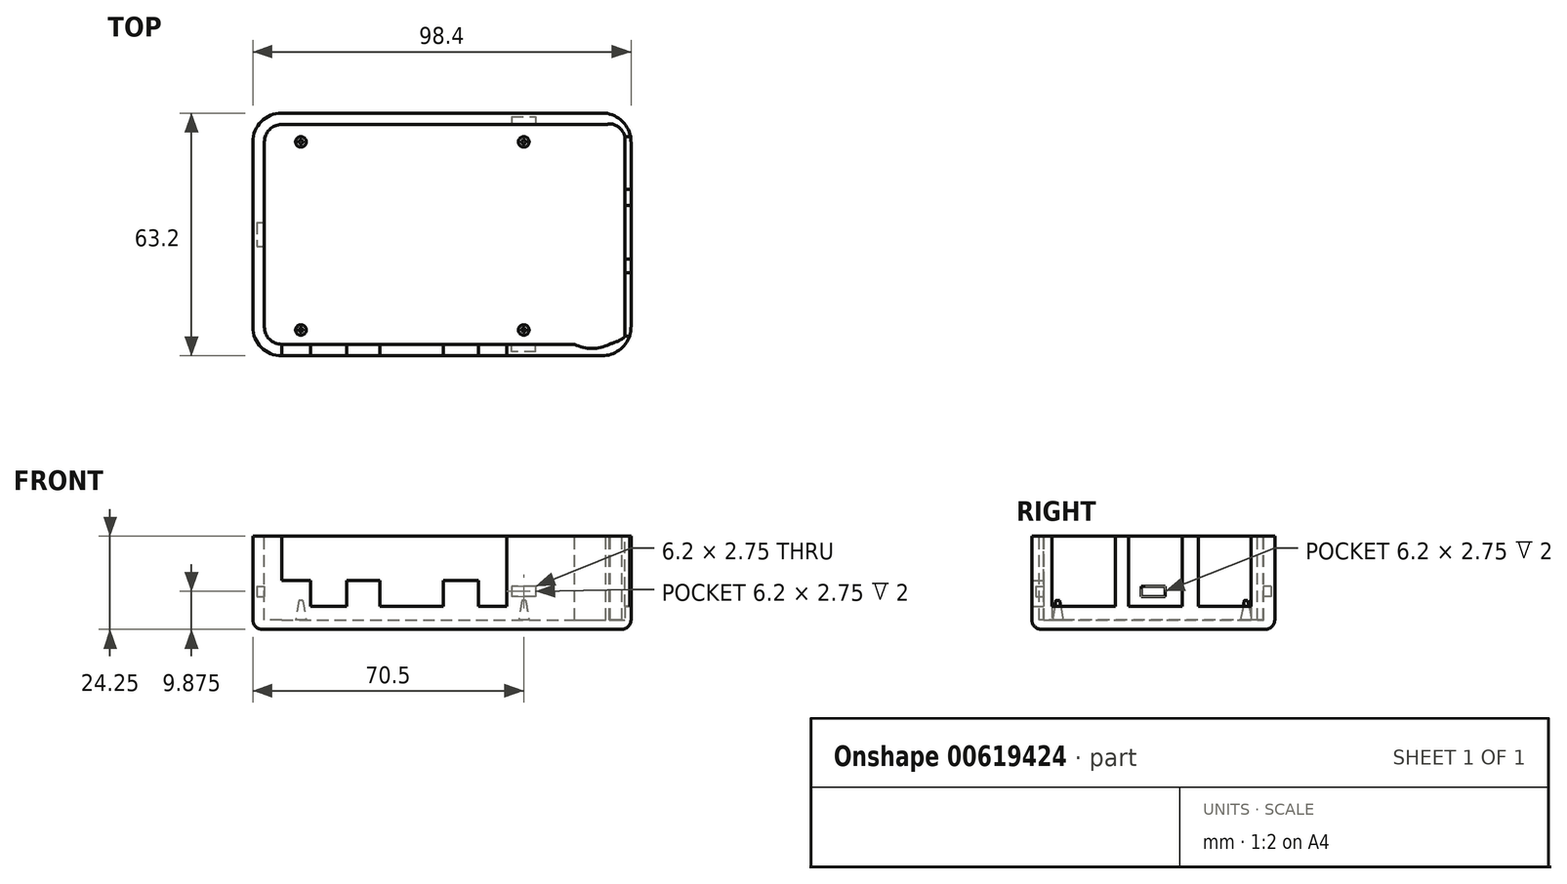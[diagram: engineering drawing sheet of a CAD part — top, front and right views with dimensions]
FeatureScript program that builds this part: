
annotation { "Feature Type Name" : "Feature", "Feature Type Description" : "" }
export const myFeature = defineFeature(function(context is Context, id is Id, definition is map)
    precondition{}
    {
        {
            var Q0;
            Q0=qCreatedBy(makeId("Top.planeOp"),FACE);
            var sketch = newSketch(context, id + "F0", { "sketchPlane" : qUnion([Q0])});
            skLineSegment(sketch, "E0.bottom", {"start": v(2.5, 0) * mm, "end": v(85.9, 0) * mm});
            skLineSegment(sketch, "E0.top", {"start": v(2.5, 53.2) * mm, "end": v(85.9, 53.2) * mm});
            skLineSegment(sketch, "E0.left", {"start": v(0, 2.5) * mm, "end": v(0, 50.7) * mm});
            skLineSegment(sketch, "E0.right", {"start": v(88.4, 2.5) * mm, "end": v(88.4, 50.7) * mm});
            skPoint(sketch, "E1.visualSharp", {"position": v(0, 53.2) * mm});
            skArc(sketch, "E1.filletArc", {"start": v(2.5, 53.2) * mm, "mid": v(0.73, 52.47) * mm, "end": v(0, 50.7) * mm});
            skPoint(sketch, "E2.visualSharp", {"position": v(0, 0) * mm});
            skArc(sketch, "E2.filletArc", {"start": v(0, 2.5) * mm, "mid": v(0.73, 0.73) * mm, "end": v(2.5, 0) * mm});
            skPoint(sketch, "E3.visualSharp", {"position": v(88.4, 0) * mm});
            skArc(sketch, "E3.filletArc", {"start": v(85.9, 0) * mm, "mid": v(87.67, 0.73) * mm, "end": v(88.4, 2.5) * mm});
            skPoint(sketch, "E4.visualSharp", {"position": v(88.4, 53.2) * mm});
            skArc(sketch, "E4.filletArc", {"start": v(88.4, 50.7) * mm, "mid": v(87.67, 52.47) * mm, "end": v(85.9, 53.2) * mm});
            skArc(sketch, "E5.0", {"start": v(2.5, 54.2) * mm, "mid": v(0.03, 53.17) * mm, "end": v(-1, 50.7) * mm});
            skLineSegment(sketch, "E5.1", {"start": v(-1, 2.5) * mm, "end": v(-1, 50.7) * mm});
            skLineSegment(sketch, "E5.2", {"start": v(2.5, 54.2) * mm, "end": v(85.9, 54.2) * mm});
            skArc(sketch, "E5.3", {"start": v(-1, 2.5) * mm, "mid": v(0.03, 0.03) * mm, "end": v(2.5, -1) * mm});
            skArc(sketch, "E5.4", {"start": v(89.4, 50.7) * mm, "mid": v(88.37, 53.17) * mm, "end": v(85.9, 54.2) * mm});
            skLineSegment(sketch, "E5.5", {"start": v(89.4, 2.5) * mm, "end": v(89.4, 50.7) * mm});
            skArc(sketch, "E5.6", {"start": v(85.9, -1) * mm, "mid": v(88.37, 0.03) * mm, "end": v(89.4, 2.5) * mm});
            skLineSegment(sketch, "E5.7", {"start": v(2.5, -1) * mm, "end": v(85.9, -1) * mm});
            skLineSegment(sketch, "E6.0", {"start": v(2.5, 58.2) * mm, "end": v(85.9, 58.2) * mm});
            skArc(sketch, "E6.1", {"start": v(93.4, 50.7) * mm, "mid": v(91.2, 56) * mm, "end": v(85.9, 58.2) * mm});
            skArc(sketch, "E6.2", {"start": v(2.5, 58.2) * mm, "mid": v(-2.8, 56) * mm, "end": v(-5, 50.7) * mm});
            skLineSegment(sketch, "E6.3", {"start": v(93.4, 2.5) * mm, "end": v(93.4, 50.7) * mm});
            skLineSegment(sketch, "E6.4", {"start": v(-5, 2.5) * mm, "end": v(-5, 50.7) * mm});
            skArc(sketch, "E6.5", {"start": v(-5, 2.5) * mm, "mid": v(-2.8, -2.8) * mm, "end": v(2.5, -5) * mm});
            skLineSegment(sketch, "E6.6", {"start": v(2.5, -5) * mm, "end": v(85.9, -5) * mm});
            skArc(sketch, "E6.7", {"start": v(85.9, -5) * mm, "mid": v(91.2, -2.8) * mm, "end": v(93.4, 2.5) * mm});
            skLineSegment(sketch, "E7", {"start": v(-2.22, 61) * mm, "end": v(-16.8, 62.79) * mm, "construction": true});
            skSolve(sketch);
        }
        {
            var Q0;
            Q0=makeQuery(id+"F0.imprint","IMPRINT",FACE,{"disambiguationData":[TD([[makeQuery(id+"F0.imprint","IMPRINT",EDGE,{"derivedFrom":sQuery(id+"F0.wireOp",EDGE,"E5.0")}),-1.0]])]});
            var Q1;
            Q1=makeQuery(id+"F0.imprint","IMPRINT",FACE,{"disambiguationData":[TD([[makeQuery(id+"F0.imprint","IMPRINT",EDGE,{"derivedFrom":sQuery(id+"F0.wireOp",EDGE,"E0.bottom")}),-1.0]])]});
            var Q2;
            Q2=makeQuery(id+"F0.imprint","IMPRINT",FACE,{"disambiguationData":[TD([[makeQuery(id+"F0.imprint","IMPRINT",EDGE,{"derivedFrom":sQuery(id+"F0.wireOp",EDGE,"E0.bottom")}),1.0]])]});
            extrude(context, id + "F1", {"entities" : qUnion([Q0, Q1, Q2]), "depth" : 21.25 * mm, "offsetDistance" : 25 * mm});
        }
        {
            var Q0;
            Q0=makeQuery(id+"F1.opExtrude","CAP_EDGE",EDGE,{"disambiguationData":[OSD([sQuery(id+"F0.wireOp",EDGE,"E6.1")])],"isStart":true});
            var Q1;
            Q1=makeQuery(id+"F1.opExtrude","CAP_EDGE",EDGE,{"disambiguationData":[OSD([sQuery(id+"F0.wireOp",EDGE,"E6.0")])],"isStart":true});
            var Q2;
            Q2=makeQuery(id+"F1.opExtrude","CAP_EDGE",EDGE,{"disambiguationData":[OSD([sQuery(id+"F0.wireOp",EDGE,"E6.3")])],"isStart":true});
            fillet(context, id + "F2", {"entities" : qUnion([Q0, Q1, Q2]), "radius" : 2.5 * mm, "tangentPropagation" : true, "allowEdgeOverflow" : false});
        }
        {
            var Q0;
            Q0=makeQuery(id+"F1.opExtrude","CAP_FACE",FACE,{"disambiguationData":[OSD([sQuery(id+"F0.wireOp",EDGE,"E6.0"),sQuery(id+"F0.wireOp",EDGE,"E6.1"),sQuery(id+"F0.wireOp",EDGE,"E6.2"),sQuery(id+"F0.wireOp",EDGE,"E6.3"),sQuery(id+"F0.wireOp",EDGE,"E6.4"),sQuery(id+"F0.wireOp",EDGE,"E6.5"),sQuery(id+"F0.wireOp",EDGE,"E6.6"),sQuery(id+"F0.wireOp",EDGE,"E6.7")])],"isStart":false});
            var sketch = newSketch(context, id + "F3", { "sketchPlane" : qUnion([Q0])});
            skLineSegment(sketch, "E8.0", {"start": v(-2, 2.5) * mm, "end": v(-2, 50.7) * mm});
            skArc(sketch, "E8.2", {"start": v(-2, 2.5) * mm, "mid": v(-0.68, -0.68) * mm, "end": v(2.5, -2) * mm});
            skLineSegment(sketch, "E8.3", {"start": v(2.5, 55.2) * mm, "end": v(86.9, 55.2) * mm});
            skLineSegment(sketch, "E8.4", {"start": v(2.5, -2) * mm, "end": v(86.9, -2) * mm});
            skPoint(sketch, "E9.visualSharp", {"position": v(-2, 55.2) * mm});
            skArc(sketch, "E9.filletArc", {"start": v(2.5, 55.2) * mm, "mid": v(-0.68, 53.88) * mm, "end": v(-2, 50.7) * mm});
            skPoint(sketch, "E10.visualSharp", {"position": v(91, 55.2) * mm});
            skArc(sketch, "E10.filletArc", {"start": v(91.4, 50.7) * mm, "mid": v(90.08, 53.88) * mm, "end": v(86.9, 55.2) * mm});
            skLineSegment(sketch, "E11", {"start": v(91.4, 2.5) * mm, "end": v(91.4, 50.7) * mm});
            skPoint(sketch, "E12.visualSharp", {"position": v(91.4, -2) * mm});
            skArc(sketch, "E12.filletArc", {"start": v(86.9, -2) * mm, "mid": v(90.08, -0.68) * mm, "end": v(91.4, 2.5) * mm});
            skSolve(sketch);
        }
        {
            var Q0;
            Q0=makeQuery(id+"F3.imprint","IMPRINT",FACE,{"disambiguationData":[TD([[makeQuery(id+"F3.imprint","IMPRINT",EDGE,{"derivedFrom":sQuery(id+"F3.wireOp",EDGE,"E8.0")}),-1.0]])]});
            extrude(context, id + "F4", {"entities" : qUnion([Q0]), "operationType" : NewBodyOperationType.REMOVE, "oppositeDirection" : true, "depth" : 18.75 * mm, "offsetDistance" : 25 * mm});
        }
        {
            var Q0;
            Q0=qCreatedBy(makeId("Top.planeOp"),FACE);
            var sketch = newSketch(context, id + "F5", { "sketchPlane" : qUnion([Q0])});
            skLineSegment(sketch, "E13.bottom", {"start": v(2.5, 0) * mm, "end": v(82.5, 0) * mm, "construction": true});
            skLineSegment(sketch, "E13.top", {"start": v(2.5, 56) * mm, "end": v(82.5, 56) * mm, "construction": true});
            skLineSegment(sketch, "E13.left", {"start": v(0, 2.5) * mm, "end": v(0, 53.5) * mm, "construction": true});
            skLineSegment(sketch, "E13.right", {"start": v(85, 2.5) * mm, "end": v(85, 53.5) * mm, "construction": true});
            skPoint(sketch, "E14.visualSharp", {"position": v(0, 56) * mm});
            skArc(sketch, "E14.filletArc", {"start": v(2.5, 56) * mm, "mid": v(0.73, 55.27) * mm, "end": v(0, 53.5) * mm, "construction": true});
            skPoint(sketch, "E15.visualSharp", {"position": v(85, 56) * mm});
            skArc(sketch, "E15.filletArc", {"start": v(85, 53.5) * mm, "mid": v(84.27, 55.27) * mm, "end": v(82.5, 56) * mm, "construction": true});
            skPoint(sketch, "E16.visualSharp", {"position": v(85, 0) * mm});
            skArc(sketch, "E16.filletArc", {"start": v(82.5, 0) * mm, "mid": v(84.27, 0.73) * mm, "end": v(85, 2.5) * mm, "construction": true});
            skPoint(sketch, "E17.visualSharp", {"position": v(0, 0) * mm});
            skArc(sketch, "E17.filletArc", {"start": v(0, 2.5) * mm, "mid": v(0.73, 0.73) * mm, "end": v(2.5, 0) * mm, "construction": true});
            skSolve(sketch);
        }
        {
            var Q0;
            Q0=makeQuery(id+"FpAsiEOdQiPqQSk_1.boolean.opBoolean","MERGE",FACE,{"derivedFrom":[makeQuery(id+"FFKmk7SwMBdEqLW_1.boolean.opBoolean","MERGE",FACE,{"derivedFrom":[makeQuery(id+"FIplIZIgQVPH8Ri_1.boolean.opBoolean","MERGE",FACE,{"derivedFrom":[makeQuery(id+"F4.boolean.opBoolean","COPY",FACE,{"derivedFrom":makeQuery(id+"F4.opExtrude","CAP_FACE",FACE,{"disambiguationData":[OSD([sQuery(id+"F3.wireOp",EDGE,"E8.0"),sQuery(id+"F3.wireOp",EDGE,"E8.1"),sQuery(id+"F3.wireOp",EDGE,"E8.2"),sQuery(id+"F3.wireOp",EDGE,"E8.3"),sQuery(id+"F3.wireOp",EDGE,"E8.4"),sQuery(id+"F3.wireOp",EDGE,"E8.5"),sQuery(id+"F3.wireOp",EDGE,"E8.6"),sQuery(id+"F3.wireOp",EDGE,"E8.7")])],"isStart":false})}),makeQuery(id+"FIplIZIgQVPH8Ri_1.opExtrude","CAP_FACE",FACE,{"disambiguationData":[OSD([sQuery(id+"FbSfHMxZk7SnYfS_1.wireOp",EDGE,"JDB0ovfy-WgS9-BKPD-cCMD-5imSfYRD1vYw.bottom"),sQuery(id+"FbSfHMxZk7SnYfS_1.wireOp",EDGE,"JDB0ovfy-WgS9-BKPD-cCMD-5imSfYRD1vYw.top"),sQuery(id+"FbSfHMxZk7SnYfS_1.wireOp",EDGE,"JDB0ovfy-WgS9-BKPD-cCMD-5imSfYRD1vYw.left"),sQuery(id+"FbSfHMxZk7SnYfS_1.wireOp",EDGE,"JDB0ovfy-WgS9-BKPD-cCMD-5imSfYRD1vYw.right")])],"isStart":false})]}),makeQuery(id+"FFKmk7SwMBdEqLW_1.opExtrude","CAP_FACE",FACE,{"disambiguationData":[OSD([sQuery(id+"FeB8znZlq4XmqRw_1.wireOp",EDGE,"MHbipOmZ-R87S-0nFG-E8Bu-bYtsTBabYH2Z.bottom"),sQuery(id+"FeB8znZlq4XmqRw_1.wireOp",EDGE,"MHbipOmZ-R87S-0nFG-E8Bu-bYtsTBabYH2Z.top"),sQuery(id+"FeB8znZlq4XmqRw_1.wireOp",EDGE,"MHbipOmZ-R87S-0nFG-E8Bu-bYtsTBabYH2Z.left"),sQuery(id+"FeB8znZlq4XmqRw_1.wireOp",EDGE,"MHbipOmZ-R87S-0nFG-E8Bu-bYtsTBabYH2Z.right")])],"isStart":false})]}),makeQuery(id+"FpAsiEOdQiPqQSk_1.opExtrude","CAP_FACE",FACE,{"disambiguationData":[OSD([sQuery(id+"Fj2ZZsyvJ0AxlN6_1.wireOp",EDGE,"Ikh8Ez46-MLNA-BZEZ-2Olo-oqhIJmUvsvPt.bottom"),sQuery(id+"Fj2ZZsyvJ0AxlN6_1.wireOp",EDGE,"Ikh8Ez46-MLNA-BZEZ-2Olo-oqhIJmUvsvPt.top"),sQuery(id+"Fj2ZZsyvJ0AxlN6_1.wireOp",EDGE,"Ikh8Ez46-MLNA-BZEZ-2Olo-oqhIJmUvsvPt.left"),sQuery(id+"Fj2ZZsyvJ0AxlN6_1.wireOp",EDGE,"Ikh8Ez46-MLNA-BZEZ-2Olo-oqhIJmUvsvPt.right")])],"isStart":false})]});
            var sketch = newSketch(context, id + "F6", { "sketchPlane" : qUnion([Q0])});
            skCircle(sketch, "E18", {"center": v(7.5, 1.7) * mm, "radius": 1.38 * mm});
            skCircle(sketch, "E19.0.1.0", {"center": v(7.5, 50.7) * mm, "radius": 1.38 * mm});
            skCircle(sketch, "E19.1.0.0", {"center": v(65.5, 1.7) * mm, "radius": 1.38 * mm});
            skCircle(sketch, "E19.1.1.0", {"center": v(65.5, 50.7) * mm, "radius": 1.38 * mm});
            skLineSegment(sketch, "E19.direction1", {"start": v(7.5, 1.7) * mm, "end": v(65.5, 1.7) * mm, "construction": true});
            skLineSegment(sketch, "E19.direction2", {"start": v(7.5, 1.7) * mm, "end": v(7.5, 50.7) * mm, "construction": true});
            skSolve(sketch);
        }
        {
            var Q0;
            Q0=makeQuery(id+"F4.boolean.opBoolean","COPY",FACE,{"derivedFrom":makeQuery(id+"F4.opExtrude","SWEPT_FACE",FACE,{"disambiguationData":[OSD([sQuery(id+"F3.wireOp",EDGE,"E8.0")])]})});
            var sketch = newSketch(context, id + "F7", { "sketchPlane" : qUnion([Q0])});
            skLineSegment(sketch, "E20.bottom", {"start": v(29.7, 11.25) * mm, "end": v(23.5, 11.25) * mm});
            skLineSegment(sketch, "E20.top", {"start": v(29.7, 8.5) * mm, "end": v(23.5, 8.5) * mm});
            skLineSegment(sketch, "E20.left", {"start": v(29.7, 11.25) * mm, "end": v(29.7, 8.5) * mm});
            skLineSegment(sketch, "E20.right", {"start": v(23.5, 11.25) * mm, "end": v(23.5, 8.5) * mm});
            skPoint(sketch, "E21", {"position": v(26.6, 11.25) * mm});
            skPoint(sketch, "E22", {"position": v(26.6, 8.5) * mm});
            skPoint(sketch, "E23", {"position": v(26.6, 21.25) * mm});
            skSolve(sketch);
        }
        {
            var Q0;
            Q0=makeQuery(id+"F7.imprint","IMPRINT",FACE,{"disambiguationData":[TD([[makeQuery(id+"F7.imprint","IMPRINT",EDGE,{"derivedFrom":sQuery(id+"F7.wireOp",EDGE,"E20.bottom")}),1.0]])]});
            extrude(context, id + "F8", {"entities" : qUnion([Q0]), "operationType" : NewBodyOperationType.REMOVE, "oppositeDirection" : true, "depth" : 2 * mm, "offsetDistance" : 25 * mm});
        }
        {
            var Q0;
            Q0=makeQuery(id+"F4.boolean.opBoolean","COPY",FACE,{"derivedFrom":makeQuery(id+"F4.opExtrude","SWEPT_FACE",FACE,{"disambiguationData":[OSD([sQuery(id+"F3.wireOp",EDGE,"E8.3")])]})});
            var sketch = newSketch(context, id + "F9", { "sketchPlane" : qUnion([Q0])});
            skLineSegment(sketch, "E24.bottom", {"start": v(62.4, 11.25) * mm, "end": v(68.6, 11.25) * mm});
            skLineSegment(sketch, "E24.top", {"start": v(62.4, 8.5) * mm, "end": v(68.6, 8.5) * mm});
            skLineSegment(sketch, "E24.left", {"start": v(62.4, 11.25) * mm, "end": v(62.4, 8.5) * mm});
            skLineSegment(sketch, "E24.right", {"start": v(68.6, 11.25) * mm, "end": v(68.6, 8.5) * mm});
            skLineSegment(sketch, "E25.0", {"start": v(64.12, 2.5) * mm, "end": v(66.88, 2.5) * mm, "construction": true});
            skPoint(sketch, "E26", {"position": v(65.5, 2.5) * mm});
            skPoint(sketch, "E27", {"position": v(65.5, 8.5) * mm});
            skSolve(sketch);
        }
        {
            var Q0;
            Q0=makeQuery(id+"F9.imprint","IMPRINT",FACE,{"disambiguationData":[TD([[makeQuery(id+"F9.imprint","IMPRINT",EDGE,{"derivedFrom":sQuery(id+"F9.wireOp",EDGE,"E24.bottom")}),-1.0]])]});
            extrude(context, id + "F10", {"entities" : qUnion([Q0]), "operationType" : NewBodyOperationType.REMOVE, "oppositeDirection" : true, "depth" : 2 * mm, "offsetDistance" : 25 * mm});
        }
        {
            var Q0;
            Q0=makeQuery(id+"FpAsiEOdQiPqQSk_1.boolean.opBoolean","MERGE",FACE,{"derivedFrom":[makeQuery(id+"FFKmk7SwMBdEqLW_1.boolean.opBoolean","MERGE",FACE,{"derivedFrom":[makeQuery(id+"FIplIZIgQVPH8Ri_1.boolean.opBoolean","MERGE",FACE,{"derivedFrom":[makeQuery(id+"F4.boolean.opBoolean","COPY",FACE,{"derivedFrom":makeQuery(id+"F4.opExtrude","CAP_FACE",FACE,{"disambiguationData":[OSD([sQuery(id+"F3.wireOp",EDGE,"E8.0"),sQuery(id+"F3.wireOp",EDGE,"E8.1"),sQuery(id+"F3.wireOp",EDGE,"E8.2"),sQuery(id+"F3.wireOp",EDGE,"E8.3"),sQuery(id+"F3.wireOp",EDGE,"E8.4"),sQuery(id+"F3.wireOp",EDGE,"E8.5"),sQuery(id+"F3.wireOp",EDGE,"E8.6"),sQuery(id+"F3.wireOp",EDGE,"E8.7")])],"isStart":false})}),makeQuery(id+"FIplIZIgQVPH8Ri_1.opExtrude","CAP_FACE",FACE,{"disambiguationData":[OSD([sQuery(id+"FbSfHMxZk7SnYfS_1.wireOp",EDGE,"JDB0ovfy-WgS9-BKPD-cCMD-5imSfYRD1vYw.bottom"),sQuery(id+"FbSfHMxZk7SnYfS_1.wireOp",EDGE,"JDB0ovfy-WgS9-BKPD-cCMD-5imSfYRD1vYw.top"),sQuery(id+"FbSfHMxZk7SnYfS_1.wireOp",EDGE,"JDB0ovfy-WgS9-BKPD-cCMD-5imSfYRD1vYw.left"),sQuery(id+"FbSfHMxZk7SnYfS_1.wireOp",EDGE,"JDB0ovfy-WgS9-BKPD-cCMD-5imSfYRD1vYw.right")])],"isStart":false})]}),makeQuery(id+"FFKmk7SwMBdEqLW_1.opExtrude","CAP_FACE",FACE,{"disambiguationData":[OSD([sQuery(id+"FeB8znZlq4XmqRw_1.wireOp",EDGE,"MHbipOmZ-R87S-0nFG-E8Bu-bYtsTBabYH2Z.bottom"),sQuery(id+"FeB8znZlq4XmqRw_1.wireOp",EDGE,"MHbipOmZ-R87S-0nFG-E8Bu-bYtsTBabYH2Z.top"),sQuery(id+"FeB8znZlq4XmqRw_1.wireOp",EDGE,"MHbipOmZ-R87S-0nFG-E8Bu-bYtsTBabYH2Z.left"),sQuery(id+"FeB8znZlq4XmqRw_1.wireOp",EDGE,"MHbipOmZ-R87S-0nFG-E8Bu-bYtsTBabYH2Z.right")])],"isStart":false})]}),makeQuery(id+"FpAsiEOdQiPqQSk_1.opExtrude","CAP_FACE",FACE,{"disambiguationData":[OSD([sQuery(id+"Fj2ZZsyvJ0AxlN6_1.wireOp",EDGE,"Ikh8Ez46-MLNA-BZEZ-2Olo-oqhIJmUvsvPt.bottom"),sQuery(id+"Fj2ZZsyvJ0AxlN6_1.wireOp",EDGE,"Ikh8Ez46-MLNA-BZEZ-2Olo-oqhIJmUvsvPt.top"),sQuery(id+"Fj2ZZsyvJ0AxlN6_1.wireOp",EDGE,"Ikh8Ez46-MLNA-BZEZ-2Olo-oqhIJmUvsvPt.left"),sQuery(id+"Fj2ZZsyvJ0AxlN6_1.wireOp",EDGE,"Ikh8Ez46-MLNA-BZEZ-2Olo-oqhIJmUvsvPt.right")])],"isStart":false})]});
            cPlane(context, id + "F11", {"entities" : qUnion([Q0]), "cplaneType" : CPlaneType.OFFSET, "offset" : 5 * mm, "width" : 150 * mm, "height" : 150 * mm});
        }
        {
            var Q0;
            Q0=qCreatedBy(id+"F11.planeOp",FACE);
            var sketch = newSketch(context, id + "F12", { "sketchPlane" : qUnion([Q0])});
            skCircle(sketch, "E28.0", {"center": v(7.5, 1.7) * mm, "radius": 1.23 * mm, "construction": true});
            skCircle(sketch, "E29", {"center": v(7.5, 1.7) * mm, "radius": 0.5 * mm});
            skCircle(sketch, "E30.0", {"center": v(7.5, 50.7) * mm, "radius": 1.23 * mm, "construction": true});
            skCircle(sketch, "E31.0", {"center": v(65.5, 50.7) * mm, "radius": 1.23 * mm, "construction": true});
            skCircle(sketch, "E32.0", {"center": v(65.5, 1.7) * mm, "radius": 1.23 * mm, "construction": true});
            skCircle(sketch, "E33", {"center": v(7.5, 50.7) * mm, "radius": 0.5 * mm});
            skCircle(sketch, "E34", {"center": v(65.5, 50.7) * mm, "radius": 0.5 * mm});
            skCircle(sketch, "E35", {"center": v(65.5, 1.7) * mm, "radius": 0.5 * mm});
            skCircle(sketch, "E36.0", {"center": v(7.5, 1.7) * mm, "radius": 1.38 * mm, "construction": true});
            skSolve(sketch);
        }
        {
            var Q1;
            Q1=makeQuery(id+"F6.imprint","IMPRINT",FACE,{"disambiguationData":[TD([[makeQuery(id+"F6.imprint","IMPRINT",EDGE,{"derivedFrom":sQuery(id+"F6.wireOp",EDGE,"E18")}),1.0]])]});
            var Q2;
            Q2=makeQuery(id+"F12.imprint","IMPRINT",FACE,{"disambiguationData":[TD([[makeQuery(id+"F12.imprint","IMPRINT",EDGE,{"derivedFrom":sQuery(id+"F12.wireOp",EDGE,"E29")}),1.0]])]});
            loft(context, id + "F13", {"operationType" : NewBodyOperationType.ADD, "sheetProfilesArray" : [{ "sheetProfileEntities" : qUnion([Q1]) }, { "sheetProfileEntities" : qUnion([Q2]) }]});
        }
        {
            var Q1;
            Q1=makeQuery(id+"F6.imprint","IMPRINT",FACE,{"disambiguationData":[TD([[makeQuery(id+"F6.imprint","IMPRINT",EDGE,{"derivedFrom":sQuery(id+"F6.wireOp",EDGE,"E19.1.0.0")}),1.0]])]});
            var Q2;
            Q2=makeQuery(id+"F12.imprint","IMPRINT",FACE,{"disambiguationData":[TD([[makeQuery(id+"F12.imprint","IMPRINT",EDGE,{"derivedFrom":sQuery(id+"F12.wireOp",EDGE,"E35")}),1.0]])]});
            loft(context, id + "F14", {"operationType" : NewBodyOperationType.ADD, "sheetProfilesArray" : [{ "sheetProfileEntities" : qUnion([Q1]) }, { "sheetProfileEntities" : qUnion([Q2]) }]});
        }
        {
            var Q1;
            Q1=makeQuery(id+"F12.imprint","IMPRINT",FACE,{"disambiguationData":[TD([[makeQuery(id+"F12.imprint","IMPRINT",EDGE,{"derivedFrom":sQuery(id+"F12.wireOp",EDGE,"E34")}),1.0]])]});
            var Q2;
            Q2=makeQuery(id+"F6.imprint","IMPRINT",FACE,{"disambiguationData":[TD([[makeQuery(id+"F6.imprint","IMPRINT",EDGE,{"derivedFrom":sQuery(id+"F6.wireOp",EDGE,"E19.1.1.0")}),1.0]])]});
            loft(context, id + "F15", {"operationType" : NewBodyOperationType.ADD, "sheetProfilesArray" : [{ "sheetProfileEntities" : qUnion([Q1]) }, { "sheetProfileEntities" : qUnion([Q2]) }]});
        }
        {
            var Q1;
            Q1=makeQuery(id+"F6.imprint","IMPRINT",FACE,{"disambiguationData":[TD([[makeQuery(id+"F6.imprint","IMPRINT",EDGE,{"derivedFrom":sQuery(id+"F6.wireOp",EDGE,"E19.0.1.0")}),1.0]])]});
            var Q2;
            Q2=makeQuery(id+"F12.imprint","IMPRINT",FACE,{"disambiguationData":[TD([[makeQuery(id+"F12.imprint","IMPRINT",EDGE,{"derivedFrom":sQuery(id+"F12.wireOp",EDGE,"E33")}),1.0]])]});
            loft(context, id + "F16", {"operationType" : NewBodyOperationType.ADD, "sheetProfilesArray" : [{ "sheetProfileEntities" : qUnion([Q1]) }, { "sheetProfileEntities" : qUnion([Q2]) }]});
        }
        {
            var Q0;
            Q0=makeQuery(id+"F1.opExtrude","CAP_FACE",FACE,{"disambiguationData":[OSD([sQuery(id+"F0.wireOp",EDGE,"E6.0"),sQuery(id+"F0.wireOp",EDGE,"E6.1"),sQuery(id+"F0.wireOp",EDGE,"E6.2"),sQuery(id+"F0.wireOp",EDGE,"E6.3"),sQuery(id+"F0.wireOp",EDGE,"E6.4"),sQuery(id+"F0.wireOp",EDGE,"E6.5"),sQuery(id+"F0.wireOp",EDGE,"E6.6"),sQuery(id+"F0.wireOp",EDGE,"E6.7")])],"isStart":false});
            var sketch = newSketch(context, id + "F17", { "sketchPlane" : qUnion([Q0])});
            skLineSegment(sketch, "E37.bottom", {"start": v(93.4, 38.37) * mm, "end": v(90.25, 38.37) * mm});
            skLineSegment(sketch, "E37.top", {"start": v(93.4, 53.7) * mm, "end": v(90.25, 53.7) * mm});
            skLineSegment(sketch, "E37.left", {"start": v(93.4, 38.36) * mm, "end": v(93.4, 53.7) * mm});
            skLineSegment(sketch, "E37.right", {"start": v(90.25, 38.36) * mm, "end": v(90.25, 53.7) * mm});
            skLineSegment(sketch, "E38.bottom", {"start": v(93.4, 20.2) * mm, "end": v(91.4, 20.2) * mm});
            skLineSegment(sketch, "E38.top", {"start": v(93.4, 34.17) * mm, "end": v(91.4, 34.17) * mm});
            skLineSegment(sketch, "E38.left", {"start": v(93.4, 20.2) * mm, "end": v(93.4, 34.16) * mm});
            skLineSegment(sketch, "E38.right", {"start": v(91.4, 20.2) * mm, "end": v(91.4, 34.16) * mm});
            skLineSegment(sketch, "E39.bottom", {"start": v(93.65, 0.15) * mm, "end": v(91.15, 0.15) * mm});
            skLineSegment(sketch, "E39.top", {"start": v(93.65, 16.68) * mm, "end": v(91.15, 16.68) * mm});
            skLineSegment(sketch, "E39.left", {"start": v(93.65, 0.15) * mm, "end": v(93.65, 16.68) * mm});
            skLineSegment(sketch, "E39.right", {"start": v(91.15, 0.15) * mm, "end": v(91.15, 16.68) * mm});
            skPoint(sketch, "E40", {"position": v(92.4, 0.15) * mm});
            skArc(sketch, "E41", {"start": v(84.7, -2) * mm, "mid": v(88.59, -1.39) * mm, "end": v(89.2, 2.5) * mm});
            skLineSegment(sketch, "E42", {"start": v(89.2, 2.5) * mm, "end": v(84.7, -2) * mm});
            skArc(sketch, "E43", {"start": v(91.4, 50.7) * mm, "mid": v(90.5, 54.3) * mm, "end": v(86.9, 55.2) * mm});
            skLineSegment(sketch, "E44", {"start": v(91.4, 50.7) * mm, "end": v(86.9, 55.2) * mm});
            skLineSegment(sketch, "E45.bottom", {"start": v(2.5, -5) * mm, "end": v(67.82, -5) * mm});
            skLineSegment(sketch, "E45.top", {"start": v(2.5, -2) * mm, "end": v(67.82, -2) * mm});
            skLineSegment(sketch, "E45.left", {"start": v(2.5, -5) * mm, "end": v(2.5, -2) * mm});
            skLineSegment(sketch, "E45.right", {"start": v(67.82, -5) * mm, "end": v(67.82, -2) * mm});
            skArc(sketch, "E46", {"start": v(78.7, -2) * mm, "mid": v(83.23, -3.13) * mm, "end": v(87.75, -2) * mm});
            skLineSegment(sketch, "E47", {"start": v(78.7, -2) * mm, "end": v(84.7, -2) * mm});
            skLineSegment(sketch, "E48", {"start": v(84.7, -2) * mm, "end": v(87.75, -2) * mm});
            skSolve(sketch);
        }
        {
            var Q0;
            Q0 = qSketchRegion(id + "F17", true);
            extrude(context, id + "F18", {"entities" : qUnion([Q0]), "operationType" : NewBodyOperationType.REMOVE, "oppositeDirection" : true, "depth" : 18.75 * mm, "offsetDistance" : 25 * mm});
        }
        {
            var Q0;
            {var subQ0=sQuery(id+"F0.wireOp",EDGE,"E6.3");Q0=makeQuery(id+"F18.boolean.opBoolean","SPLIT",FACE,{"disambiguationData":[TD([makeQuery(id+"F18.opExtrude","SWEPT_FACE",FACE,{"disambiguationData":[OSD([sQuery(id+"F17.wireOp",EDGE,"E37.bottom")])]})])],"derivedFrom":makeQuery(id+"F1.opExtrude","CAP_FACE",FACE,{"disambiguationData":[OSD([sQuery(id+"F0.wireOp",EDGE,"E6.0"),sQuery(id+"F0.wireOp",EDGE,"E6.1"),sQuery(id+"F0.wireOp",EDGE,"E6.2"),subQ0,sQuery(id+"F0.wireOp",EDGE,"E6.4"),sQuery(id+"F0.wireOp",EDGE,"E6.5"),sQuery(id+"F0.wireOp",EDGE,"E6.6"),sQuery(id+"F0.wireOp",EDGE,"E6.7")])],"isStart":false})});}
            var sketch = newSketch(context, id + "F19", { "sketchPlane" : qUnion([Q0])});
            skLineSegment(sketch, "E49.bottom", {"start": v(89.34, 41.09) * mm, "end": v(91.82, 41.09) * mm});
            skLineSegment(sketch, "E49.top", {"start": v(89.34, 12.26) * mm, "end": v(91.82, 12.26) * mm});
            skLineSegment(sketch, "E49.left", {"start": v(89.34, 41.09) * mm, "end": v(89.34, 12.26) * mm});
            skLineSegment(sketch, "E49.right", {"start": v(91.82, 41.09) * mm, "end": v(91.82, 12.26) * mm});
            skLineSegment(sketch, "E50.bottom", {"start": v(96.82, 12.26) * mm, "end": v(92.82, 12.26) * mm});
            skLineSegment(sketch, "E50.top", {"start": v(96.82, 41.07) * mm, "end": v(92.82, 41.07) * mm});
            skLineSegment(sketch, "E50.left", {"start": v(96.82, 12.26) * mm, "end": v(96.82, 41.07) * mm});
            skLineSegment(sketch, "E50.right", {"start": v(92.82, 12.26) * mm, "end": v(92.82, 41.07) * mm});
            skSolve(sketch);
        }
        {
            var Q0;
            Q0 = qSketchRegion(id + "F19", true);
            extrude(context, id + "F20", {"entities" : qUnion([Q0]), "operationType" : NewBodyOperationType.REMOVE, "oppositeDirection" : true, "depth" : 18.75 * mm, "offsetDistance" : 25 * mm});
        }
        {
            var Q0;
            Q0=makeQuery(id+"F20.boolean.opBoolean","MERGE",FACE,{"derivedFrom":[makeQuery(id+"F18.boolean.opBoolean","MERGE",FACE,{"derivedFrom":[makeQuery(id+"F4.boolean.opBoolean","COPY",FACE,{"derivedFrom":makeQuery(id+"F4.opExtrude","CAP_FACE",FACE,{"disambiguationData":[OSD([sQuery(id+"F3.wireOp",EDGE,"E8.0"),sQuery(id+"F3.wireOp",EDGE,"E8.2"),sQuery(id+"F3.wireOp",EDGE,"E8.3"),sQuery(id+"F3.wireOp",EDGE,"E8.4"),sQuery(id+"F3.wireOp",EDGE,"E9.filletArc"),sQuery(id+"F3.wireOp",EDGE,"E10.filletArc"),sQuery(id+"F3.wireOp",EDGE,"E11"),sQuery(id+"F3.wireOp",EDGE,"E12.filletArc")])],"isStart":false})}),makeQuery(id+"F18.opExtrude","CAP_FACE",FACE,{"disambiguationData":[OSD([sQuery(id+"F17.wireOp",EDGE,"E37.bottom"),sQuery(id+"F17.wireOp",EDGE,"E37.top"),sQuery(id+"F17.wireOp",EDGE,"E37.left"),sQuery(id+"F17.wireOp",EDGE,"E37.right"),sQuery(id+"F17.wireOp",EDGE,"E43"),sQuery(id+"F17.wireOp",EDGE,"E44")])],"isStart":false}),makeQuery(id+"F18.opExtrude","CAP_FACE",FACE,{"disambiguationData":[OSD([sQuery(id+"F17.wireOp",EDGE,"E38.bottom"),sQuery(id+"F17.wireOp",EDGE,"E38.top"),sQuery(id+"F17.wireOp",EDGE,"E38.left"),sQuery(id+"F17.wireOp",EDGE,"E38.right")])],"isStart":false}),makeQuery(id+"F18.opExtrude","CAP_FACE",FACE,{"disambiguationData":[OSD([sQuery(id+"F17.wireOp",EDGE,"E39.bottom"),sQuery(id+"F17.wireOp",EDGE,"E39.top"),sQuery(id+"F17.wireOp",EDGE,"E39.left"),sQuery(id+"F17.wireOp",EDGE,"E39.right"),sQuery(id+"F17.wireOp",EDGE,"E41"),sQuery(id+"F17.wireOp",EDGE,"E42"),sQuery(id+"F17.wireOp",EDGE,"E46"),sQuery(id+"F17.wireOp",EDGE,"E47")])],"isStart":false}),makeQuery(id+"F18.opExtrude","CAP_FACE",FACE,{"disambiguationData":[OSD([sQuery(id+"F17.wireOp",EDGE,"E45.bottom"),sQuery(id+"F17.wireOp",EDGE,"E45.top"),sQuery(id+"F17.wireOp",EDGE,"E45.left"),sQuery(id+"F17.wireOp",EDGE,"E45.right")])],"isStart":false})]}),makeQuery(id+"F20.opExtrude","CAP_FACE",FACE,{"disambiguationData":[OSD([sQuery(id+"F19.wireOp",EDGE,"E49.bottom"),sQuery(id+"F19.wireOp",EDGE,"E49.top"),sQuery(id+"F19.wireOp",EDGE,"E49.left"),sQuery(id+"F19.wireOp",EDGE,"E49.right")])],"isStart":false}),makeQuery(id+"F20.opExtrude","CAP_FACE",FACE,{"disambiguationData":[OSD([sQuery(id+"F19.wireOp",EDGE,"E50.bottom"),sQuery(id+"F19.wireOp",EDGE,"E50.top"),sQuery(id+"F19.wireOp",EDGE,"E50.left"),sQuery(id+"F19.wireOp",EDGE,"E50.right")])],"isStart":false})]});
            var sketch = newSketch(context, id + "F21", { "sketchPlane" : qUnion([Q0])});
            skLineSegment(sketch, "E51.bottom", {"start": v(91.82, 34.17) * mm, "end": v(92.82, 34.17) * mm});
            skLineSegment(sketch, "E51.top", {"start": v(91.82, 20.2) * mm, "end": v(92.82, 20.2) * mm});
            skLineSegment(sketch, "E51.left", {"start": v(91.82, 34.17) * mm, "end": v(91.82, 20.2) * mm});
            skLineSegment(sketch, "E51.right", {"start": v(92.82, 34.17) * mm, "end": v(92.82, 20.2) * mm});
            skLineSegment(sketch, "E52.bottom", {"start": v(91.82, 16.68) * mm, "end": v(92.82, 16.68) * mm});
            skLineSegment(sketch, "E52.top", {"start": v(91.82, 0.15) * mm, "end": v(92.82, 0.15) * mm});
            skLineSegment(sketch, "E52.left", {"start": v(91.82, 16.68) * mm, "end": v(91.82, 0.15) * mm});
            skLineSegment(sketch, "E52.right", {"start": v(92.82, 16.68) * mm, "end": v(92.82, 0.15) * mm});
            skLineSegment(sketch, "E53.bottom", {"start": v(91.82, 38.37) * mm, "end": v(92.82, 38.37) * mm});
            skLineSegment(sketch, "E53.top", {"start": v(91.82, 49.7) * mm, "end": v(92.82, 49.7) * mm});
            skLineSegment(sketch, "E53.left", {"start": v(91.82, 38.37) * mm, "end": v(91.82, 49.7) * mm});
            skLineSegment(sketch, "E53.right", {"start": v(92.82, 38.37) * mm, "end": v(92.82, 49.7) * mm});
            skSolve(sketch);
        }
        {
            var Q0;
            Q0=makeQuery(id+"F21.imprint","IMPRINT",FACE,{"disambiguationData":[TD([[makeQuery(id+"F21.imprint","IMPRINT",EDGE,{"derivedFrom":sQuery(id+"F21.wireOp",EDGE,"E51.left")}),-1.0]])]});
            var sketch = newSketch(context, id + "F22", { "sketchPlane" : qUnion([Q0])});
            skLineSegment(sketch, "E54.0", {"start": v(92.77, 53.7) * mm, "end": v(90.98, 53.7) * mm});
            skLineSegment(sketch, "E55.top", {"start": v(92.77, 51.5) * mm, "end": v(90.98, 51.5) * mm});
            skLineSegment(sketch, "E55.left", {"start": v(92.77, 53.7) * mm, "end": v(92.77, 51.5) * mm});
            skLineSegment(sketch, "E55.right", {"start": v(90.98, 53.7) * mm, "end": v(90.98, 51.5) * mm});
            skSolve(sketch);
        }
        {
            var Q0;
            Q0 = qSketchRegion(id + "F21", true);
            extrude(context, id + "F23", {"entities" : qUnion([Q0]), "operationType" : NewBodyOperationType.ADD, "depth" : 3.5 * mm, "offsetDistance" : 25 * mm});
        }
        {
            var Q0;
            Q0=makeQuery(id+"F18.boolean.opBoolean","COPY",FACE,{"derivedFrom":makeQuery(id+"F18.opExtrude","SWEPT_FACE",FACE,{"disambiguationData":[OSD([sQuery(id+"F17.wireOp",EDGE,"E45.right")])]})});
            extrude(context, id + "F24", {"entities" : qUnion([Q0]), "operationType" : NewBodyOperationType.ADD, "depth" : 6.5 * mm, "offsetDistance" : 25 * mm});
        }
        {
            var Q0;
            {var subQ0=sQuery(id+"F3.wireOp",EDGE,"E8.4");Q0=makeQuery(id+"F24.boolean.opBoolean","MERGE",FACE,{"derivedFrom":[makeQuery(id+"F4.boolean.opBoolean","COPY",FACE,{"derivedFrom":makeQuery(id+"F4.opExtrude","SWEPT_FACE",FACE,{"disambiguationData":[OSD([subQ0])]})}),makeQuery(id+"F24.opExtrude","SWEPT_FACE",FACE,{"disambiguationData":[OSD([subQ0,sQuery(id+"F17.wireOp",EDGE,"E45.top"),sQuery(id+"F17.wireOp",EDGE,"E45.right")])]})]});}
            var sketch = newSketch(context, id + "F25", { "sketchPlane" : qUnion([Q0])});
            skLineSegment(sketch, "E56.bottom", {"start": v(-68.6, 11.25) * mm, "end": v(-62.4, 11.25) * mm});
            skLineSegment(sketch, "E56.top", {"start": v(-68.6, 8.5) * mm, "end": v(-62.4, 8.5) * mm});
            skLineSegment(sketch, "E56.left", {"start": v(-68.6, 11.25) * mm, "end": v(-68.6, 8.5) * mm});
            skLineSegment(sketch, "E56.right", {"start": v(-62.4, 11.25) * mm, "end": v(-62.4, 8.5) * mm});
            skPoint(sketch, "E57", {"position": v(-65.5, 8.5) * mm});
            skLineSegment(sketch, "E58.0", {"start": v(-66, 7.5) * mm, "end": v(-65, 7.5) * mm, "construction": true});
            skPoint(sketch, "E59", {"position": v(-65.5, 7.5) * mm});
            skSolve(sketch);
        }
        {
            var Q0;
            Q0 = qSketchRegion(id + "F25", true);
            extrude(context, id + "F26", {"entities" : qUnion([Q0]), "operationType" : NewBodyOperationType.REMOVE, "oppositeDirection" : true, "depth" : 2 * mm, "offsetDistance" : 25 * mm});
        }
        {
            var Q0;
            Q0=makeQuery(id+"F18.boolean.opBoolean","COPY",FACE,{"derivedFrom":makeQuery(id+"F18.opExtrude","SWEPT_FACE",FACE,{"disambiguationData":[OSD([sQuery(id+"F17.wireOp",EDGE,"E37.top")])]})});
            extrude(context, id + "F27", {"entities" : qUnion([Q0]), "operationType" : NewBodyOperationType.ADD, "depth" : 1.7 * mm, "offsetDistance" : 25 * mm});
        }
        {
            var Q0;
            Q0=makeQuery(id+"F23.opExtrude","SWEPT_FACE",FACE,{"disambiguationData":[OSD([sQuery(id+"F21.wireOp",EDGE,"E53.top")])]});
            var Q1;
            Q1=makeQuery(id+"F27.opExtrude","CAP_FACE",FACE,{"disambiguationData":[OSD([sQuery(id+"F17.wireOp",EDGE,"E37.top")])],"isStart":false});
            extrude(context, id + "F28", {"entities" : qUnion([Q0]), "operationType" : NewBodyOperationType.ADD, "endBound" : BoundingType.UP_TO_SURFACE, "depth" : 25 * mm, "endBoundEntityFace" : qUnion([Q1]), "offsetDistance" : 25 * mm});
        }
        {
            var Q0;
            {var subQ0=sQuery(id+"F21.wireOp",EDGE,"E53.right");var subQ2=sQuery(id+"F17.wireOp",EDGE,"E38.bottom");var subQ4=sQuery(id+"F17.wireOp",EDGE,"E37.bottom");var subQ7=sQuery(id+"F19.wireOp",EDGE,"E50.right");var subQ14=makeQuery(id+"F20.opExtrude","SWEPT_FACE",FACE,{"disambiguationData":[OSD([subQ7])]});Q0=makeQuery(id+"F28.boolean.opBoolean","MERGE",FACE,{"derivedFrom":[makeQuery(id+"F23.boolean.opBoolean","MERGE",FACE,{"derivedFrom":[makeQuery(id+"F20.boolean.opBoolean","COPY",FACE,{"disambiguationData":[TD([makeQuery(id+"F18.boolean.opBoolean","COPY",FACE,{"derivedFrom":makeQuery(id+"F18.opExtrude","SWEPT_FACE",FACE,{"disambiguationData":[OSD([subQ4])]})})])],"derivedFrom":subQ14}),makeQuery(id+"F20.boolean.opBoolean","COPY",FACE,{"disambiguationData":[TD([makeQuery(id+"F18.boolean.opBoolean","COPY",FACE,{"derivedFrom":makeQuery(id+"F18.opExtrude","SWEPT_FACE",FACE,{"disambiguationData":[OSD([subQ2])]})})])],"derivedFrom":subQ14}),makeQuery(id+"F23.opExtrude","SWEPT_FACE",FACE,{"disambiguationData":[OSD([sQuery(id+"F21.wireOp",EDGE,"E51.right")])]}),makeQuery(id+"F23.opExtrude","SWEPT_FACE",FACE,{"disambiguationData":[OSD([sQuery(id+"F21.wireOp",EDGE,"E52.right")])]}),makeQuery(id+"F23.opExtrude","SWEPT_FACE",FACE,{"disambiguationData":[OSD([subQ0])]})]}),makeQuery(id+"F28.opExtrude","SWEPT_FACE",FACE,{"disambiguationData":[OSD([sQuery(id+"F21.wireOp",EDGE,"E53.top"),subQ0])]})]});}
            var sketch = newSketch(context, id + "F29", { "sketchPlane" : qUnion([Q0])});
            skLineSegment(sketch, "E60.bottom", {"start": v(-14.86, 32.45) * mm, "end": v(63.42, 32.45) * mm});
            skLineSegment(sketch, "E60.top", {"start": v(-14.86, -6.91) * mm, "end": v(63.42, -6.91) * mm});
            skLineSegment(sketch, "E60.left", {"start": v(-14.86, 32.45) * mm, "end": v(-14.86, -6.91) * mm});
            skLineSegment(sketch, "E60.right", {"start": v(63.42, 32.45) * mm, "end": v(63.42, -6.91) * mm});
            skSolve(sketch);
        }
        {
            var Q0;
            Q0=makeQuery(id+"F22.imprint","IMPRINT",FACE,{"disambiguationData":[TD([[makeQuery(id+"F22.imprint","IMPRINT",EDGE,{"derivedFrom":sQuery(id+"F22.wireOp",EDGE,"E55.top")}),1.0]])]});
            var sketch = newSketch(context, id + "F30", { "sketchPlane" : qUnion([Q0])});
            skLineSegment(sketch, "E61.0", {"start": v(2.5, -5) * mm, "end": v(2.5, -2) * mm, "construction": true});
            skLineSegment(sketch, "E62.0", {"start": v(61.32, -5) * mm, "end": v(61.32, -2) * mm, "construction": true});
            skLineSegment(sketch, "E63.bottom", {"start": v(2.5, -5) * mm, "end": v(61.32, -5) * mm});
            skLineSegment(sketch, "E63.top", {"start": v(2.5, -2) * mm, "end": v(61.32, -2) * mm});
            skLineSegment(sketch, "E63.left", {"start": v(2.5, -5) * mm, "end": v(2.5, -2) * mm});
            skLineSegment(sketch, "E63.right", {"start": v(61.32, -5) * mm, "end": v(61.32, -2) * mm});
            skSolve(sketch);
        }
        {
            var Q0;
            Q0=makeQuery(id+"F30.imprint","IMPRINT",FACE,{"disambiguationData":[TD([[makeQuery(id+"F30.imprint","IMPRINT",EDGE,{"derivedFrom":sQuery(id+"F30.wireOp",EDGE,"E63.bottom")}),1.0]])]});
            extrude(context, id + "F31", {"entities" : qUnion([Q0]), "operationType" : NewBodyOperationType.ADD, "depth" : 3.5 * mm, "offsetDistance" : 25 * mm});
        }
        {
            var Q0;
            Q0=makeQuery(id+"F31.opExtrude","CAP_FACE",FACE,{"disambiguationData":[OSD([sQuery(id+"F30.wireOp",EDGE,"E63.bottom"),sQuery(id+"F30.wireOp",EDGE,"E63.top"),sQuery(id+"F30.wireOp",EDGE,"E63.left"),sQuery(id+"F30.wireOp",EDGE,"E63.right")])],"isStart":false});
            var sketch = newSketch(context, id + "F32", { "sketchPlane" : qUnion([Q0])});
            skLineSegment(sketch, "E64.bottom", {"start": v(61.32, -5) * mm, "end": v(61.1, -5) * mm});
            skLineSegment(sketch, "E64.top", {"start": v(61.32, -2) * mm, "end": v(61.1, -2) * mm});
            skLineSegment(sketch, "E64.left", {"start": v(61.32, -5) * mm, "end": v(61.32, -2) * mm});
            skLineSegment(sketch, "E64.right", {"start": v(61.1, -5) * mm, "end": v(61.1, -2) * mm});
            skLineSegment(sketch, "E65.bottom", {"start": v(44.5, -5) * mm, "end": v(53.7, -5) * mm});
            skLineSegment(sketch, "E65.top", {"start": v(44.5, -2) * mm, "end": v(53.7, -2) * mm});
            skLineSegment(sketch, "E65.left", {"start": v(44.5, -5) * mm, "end": v(44.5, -2) * mm});
            skLineSegment(sketch, "E65.right", {"start": v(53.7, -5) * mm, "end": v(53.7, -2) * mm});
            skLineSegment(sketch, "E66.bottom", {"start": v(19.43, -5) * mm, "end": v(28.1, -5) * mm});
            skLineSegment(sketch, "E66.top", {"start": v(19.43, -2) * mm, "end": v(28.1, -2) * mm});
            skLineSegment(sketch, "E66.left", {"start": v(19.43, -5) * mm, "end": v(19.43, -2) * mm});
            skLineSegment(sketch, "E66.right", {"start": v(28.1, -5) * mm, "end": v(28.1, -2) * mm});
            skLineSegment(sketch, "E67.bottom", {"start": v(2.5, -5) * mm, "end": v(10.03, -5) * mm});
            skLineSegment(sketch, "E67.top", {"start": v(2.5, -2) * mm, "end": v(10.03, -2) * mm});
            skLineSegment(sketch, "E67.left", {"start": v(2.5, -5) * mm, "end": v(2.5, -2) * mm});
            skLineSegment(sketch, "E67.right", {"start": v(10.03, -5) * mm, "end": v(10.03, -2) * mm});
            skSolve(sketch);
        }
        {
            var Q0;
            Q0 = qSketchRegion(id + "F32", true);
            extrude(context, id + "F33", {"entities" : qUnion([Q0]), "operationType" : NewBodyOperationType.ADD, "depth" : 6.7 * mm, "offsetDistance" : 25 * mm});
        }
        {
            var Q0;
            Q0=makeQuery(id+"F33.opExtrude","CAP_FACE",FACE,{"disambiguationData":[OSD([sQuery(id+"F32.wireOp",EDGE,"E64.bottom"),sQuery(id+"F32.wireOp",EDGE,"E64.top"),sQuery(id+"F32.wireOp",EDGE,"E64.left"),sQuery(id+"F32.wireOp",EDGE,"E64.right")])],"isStart":false});
            var Q1;
            {var subQ0=sQuery(id+"F17.wireOp",EDGE,"E45.right");var subQ1=sQuery(id+"F0.wireOp",EDGE,"E6.7");var subQ2=sQuery(id+"F0.wireOp",EDGE,"E6.6");Q1=makeQuery(id+"F24.boolean.opBoolean","MERGE",FACE,{"derivedFrom":[makeQuery(id+"F18.boolean.opBoolean","SPLIT",FACE,{"disambiguationData":[TD([makeQuery(id+"F1.opExtrude","SWEPT_FACE",FACE,{"disambiguationData":[OSD([subQ2])]})])],"derivedFrom":makeQuery(id+"F1.opExtrude","CAP_FACE",FACE,{"disambiguationData":[OSD([sQuery(id+"F0.wireOp",EDGE,"E6.0"),sQuery(id+"F0.wireOp",EDGE,"E6.1"),sQuery(id+"F0.wireOp",EDGE,"E6.2"),sQuery(id+"F0.wireOp",EDGE,"E6.3"),sQuery(id+"F0.wireOp",EDGE,"E6.4"),sQuery(id+"F0.wireOp",EDGE,"E6.5"),subQ2,subQ1])],"isStart":false})}),makeQuery(id+"F24.opExtrude","SWEPT_FACE",FACE,{"disambiguationData":[OSD([subQ0]),TDD([makeQuery(id+"F18.boolean.opBoolean","COPY",EDGE,{"derivedFrom":makeQuery(id+"F18.opExtrude","CAP_EDGE",EDGE,{"disambiguationData":[OSD([subQ0])],"isStart":true})})])]})]});}
            extrude(context, id + "F34", {"entities" : qUnion([Q0]), "operationType" : NewBodyOperationType.ADD, "endBound" : BoundingType.UP_TO_SURFACE, "depth" : 25 * mm, "endBoundEntityFace" : qUnion([Q1]), "offsetDistance" : 25 * mm});
        }
        {
            var Q0;
            {var subQ0=sQuery(id+"F17.wireOp",EDGE,"E37.top");var subQ1=sQuery(id+"F0.wireOp",EDGE,"E6.5");var subQ2=sQuery(id+"F0.wireOp",EDGE,"E6.0");var subQ3=sQuery(id+"F0.wireOp",EDGE,"E6.1");var subQ4=sQuery(id+"F0.wireOp",EDGE,"E6.2");var subQ5=sQuery(id+"F0.wireOp",EDGE,"E6.4");Q0=makeQuery(id+"F27.boolean.opBoolean","MERGE",FACE,{"derivedFrom":[makeQuery(id+"F18.boolean.opBoolean","SPLIT",FACE,{"disambiguationData":[TD([makeQuery(id+"F1.opExtrude","SWEPT_FACE",FACE,{"disambiguationData":[OSD([subQ2])]})])],"derivedFrom":makeQuery(id+"F1.opExtrude","CAP_FACE",FACE,{"disambiguationData":[OSD([subQ2,subQ3,subQ4,sQuery(id+"F0.wireOp",EDGE,"E6.3"),subQ5,subQ1,sQuery(id+"F0.wireOp",EDGE,"E6.6"),sQuery(id+"F0.wireOp",EDGE,"E6.7")])],"isStart":false})}),makeQuery(id+"F27.opExtrude","SWEPT_FACE",FACE,{"disambiguationData":[OSD([subQ0]),TDD([makeQuery(id+"F18.boolean.opBoolean","COPY",EDGE,{"derivedFrom":makeQuery(id+"F18.opExtrude","CAP_EDGE",EDGE,{"disambiguationData":[OSD([subQ0])],"isStart":true})})])]})]});}
            var Q1;
            {var subQ0=sQuery(id+"F17.wireOp",EDGE,"E45.right");var subQ1=sQuery(id+"F0.wireOp",EDGE,"E6.7");var subQ2=sQuery(id+"F0.wireOp",EDGE,"E6.6");Q1=makeQuery(id+"F34.boolean.opBoolean","MERGE",FACE,{"derivedFrom":[makeQuery(id+"F24.boolean.opBoolean","MERGE",FACE,{"derivedFrom":[makeQuery(id+"F18.boolean.opBoolean","SPLIT",FACE,{"disambiguationData":[TD([makeQuery(id+"F1.opExtrude","SWEPT_FACE",FACE,{"disambiguationData":[OSD([subQ2])]})])],"derivedFrom":makeQuery(id+"F1.opExtrude","CAP_FACE",FACE,{"disambiguationData":[OSD([sQuery(id+"F0.wireOp",EDGE,"E6.0"),sQuery(id+"F0.wireOp",EDGE,"E6.1"),sQuery(id+"F0.wireOp",EDGE,"E6.2"),sQuery(id+"F0.wireOp",EDGE,"E6.3"),sQuery(id+"F0.wireOp",EDGE,"E6.4"),sQuery(id+"F0.wireOp",EDGE,"E6.5"),subQ2,subQ1])],"isStart":false})}),makeQuery(id+"F24.opExtrude","SWEPT_FACE",FACE,{"disambiguationData":[OSD([subQ0]),TDD([makeQuery(id+"F18.boolean.opBoolean","COPY",EDGE,{"derivedFrom":makeQuery(id+"F18.opExtrude","CAP_EDGE",EDGE,{"disambiguationData":[OSD([subQ0])],"isStart":true})})])]})]}),makeQuery(id+"F34.opExtrude","CAP_FACE",FACE,{"disambiguationData":[OSD([sQuery(id+"F32.wireOp",EDGE,"E64.bottom"),sQuery(id+"F32.wireOp",EDGE,"E64.top"),sQuery(id+"F32.wireOp",EDGE,"E64.left"),sQuery(id+"F32.wireOp",EDGE,"E64.right")])],"isStart":false})]});}
            var Q2;
            {var subQ0=sQuery(id+"F0.wireOp",EDGE,"E6.3");Q2=makeQuery(id+"F18.boolean.opBoolean","SPLIT",FACE,{"disambiguationData":[TD([makeQuery(id+"F18.opExtrude","SWEPT_FACE",FACE,{"disambiguationData":[OSD([sQuery(id+"F17.wireOp",EDGE,"E38.bottom")])]})])],"derivedFrom":makeQuery(id+"F1.opExtrude","CAP_FACE",FACE,{"disambiguationData":[OSD([sQuery(id+"F0.wireOp",EDGE,"E6.0"),sQuery(id+"F0.wireOp",EDGE,"E6.1"),sQuery(id+"F0.wireOp",EDGE,"E6.2"),subQ0,sQuery(id+"F0.wireOp",EDGE,"E6.4"),sQuery(id+"F0.wireOp",EDGE,"E6.5"),sQuery(id+"F0.wireOp",EDGE,"E6.6"),sQuery(id+"F0.wireOp",EDGE,"E6.7")])],"isStart":false})});}
            var Q3;
            {var subQ0=sQuery(id+"F0.wireOp",EDGE,"E6.3");Q3=makeQuery(id+"F18.boolean.opBoolean","SPLIT",FACE,{"disambiguationData":[TD([makeQuery(id+"F18.opExtrude","SWEPT_FACE",FACE,{"disambiguationData":[OSD([sQuery(id+"F17.wireOp",EDGE,"E37.bottom")])]})])],"derivedFrom":makeQuery(id+"F1.opExtrude","CAP_FACE",FACE,{"disambiguationData":[OSD([sQuery(id+"F0.wireOp",EDGE,"E6.0"),sQuery(id+"F0.wireOp",EDGE,"E6.1"),sQuery(id+"F0.wireOp",EDGE,"E6.2"),subQ0,sQuery(id+"F0.wireOp",EDGE,"E6.4"),sQuery(id+"F0.wireOp",EDGE,"E6.5"),sQuery(id+"F0.wireOp",EDGE,"E6.6"),sQuery(id+"F0.wireOp",EDGE,"E6.7")])],"isStart":false})});}
            extrude(context, id + "F35", {"entities" : qUnion([Q0, Q1, Q2, Q3]), "operationType" : NewBodyOperationType.ADD, "depth" : 3 * mm, "offsetDistance" : 25 * mm});
        }
        {
            var Q0;
            Q0=makeQuery(id+"F22.imprint","IMPRINT",FACE,{"disambiguationData":[TD([[makeQuery(id+"F22.imprint","IMPRINT",EDGE,{"derivedFrom":sQuery(id+"F22.wireOp",EDGE,"E55.top")}),1.0]])]});
            var sketch = newSketch(context, id + "F36", { "sketchPlane" : qUnion([Q0])});
            skLineSegment(sketch, "E68.0", {"start": v(92.77, 52) * mm, "end": v(92.82, 52) * mm});
            skArc(sketch, "E69.0", {"start": v(93.4, 50.7) * mm, "mid": v(93.24, 52.23) * mm, "end": v(92.77, 53.7) * mm});
            skLineSegment(sketch, "E70", {"start": v(92.77, 52) * mm, "end": v(92.77, 53.7) * mm});
            skLineSegment(sketch, "E71.0", {"start": v(93.02, 0.15) * mm, "end": v(92.82, 0.15) * mm});
            skArc(sketch, "E72.0", {"start": v(93.4, 2.5) * mm, "mid": v(93.3, 1.3) * mm, "end": v(93.02, 0.15) * mm});
            skLineSegment(sketch, "E73", {"start": v(92.82, 0.15) * mm, "end": v(92.82, 52) * mm});
            skLineSegment(sketch, "E74", {"start": v(93.4, 50.7) * mm, "end": v(93.4, 2.5) * mm});
            skSolve(sketch);
        }
        {
            var Q0;
            {var subQ7=sQuery(id+"F36.wireOp",EDGE,"E68.0");Q0=makeQuery(id+"F36.imprint","IMPRINT",FACE,{"disambiguationData":[TD([[makeQuery(id+"F36.imprint","IMPRINT",EDGE,{"derivedFrom":subQ7}),1.0]])]});}
            extrude(context, id + "F37", {"entities" : qUnion([Q0]), "operationType" : NewBodyOperationType.ADD, "depth" : 3.5 * mm, "offsetDistance" : 25 * mm});
        }
        {
            var Q0;
            {var subQ0=sQuery(id+"F17.wireOp",EDGE,"E39.right");Q0=makeQuery(id+"F35.boolean.opBoolean","MERGE",FACE,{"derivedFrom":[makeQuery(id+"F18.boolean.opBoolean","COPY",FACE,{"derivedFrom":makeQuery(id+"F18.opExtrude","SWEPT_FACE",FACE,{"disambiguationData":[OSD([subQ0])]})}),makeQuery(id+"F35.opExtrude","SWEPT_FACE",FACE,{"disambiguationData":[OSD([subQ0])]})]});}
            var Q1;
            {var subQ0=sQuery(id+"F3.wireOp",EDGE,"E12.filletArc");Q1=makeQuery(id+"F35.boolean.opBoolean","MERGE",FACE,{"derivedFrom":[makeQuery(id+"F4.boolean.opBoolean","COPY",FACE,{"derivedFrom":makeQuery(id+"F4.opExtrude","SWEPT_FACE",FACE,{"disambiguationData":[OSD([subQ0])]})}),makeQuery(id+"F35.opExtrude","SWEPT_FACE",FACE,{"disambiguationData":[OSD([subQ0])]})]});}
            extrude(context, id + "F38", {"entities" : qUnion([Q0]), "operationType" : NewBodyOperationType.REMOVE, "endBound" : BoundingType.UP_TO_SURFACE, "oppositeDirection" : true, "depth" : 2 * mm, "endBoundEntityFace" : qUnion([Q1]), "offsetDistance" : 25 * mm});
        }
        {
            var Q0;
            {var subQ0=sQuery(id+"F17.wireOp",EDGE,"E37.top");var subQ1=sQuery(id+"F0.wireOp",EDGE,"E6.1");Q0=makeQuery(id+"F35.boolean.opBoolean","MERGE",FACE,{"derivedFrom":[makeQuery(id+"F27.opExtrude","SWEPT_FACE",FACE,{"disambiguationData":[OSD([subQ1,subQ0])]}),makeQuery(id+"F35.opExtrude","SWEPT_FACE",FACE,{"disambiguationData":[OSD([subQ1,subQ0])]})]});}
            var Q1;
            {var subQ0=sQuery(id+"F0.wireOp",EDGE,"E6.1");Q1=makeQuery(id+"F37.boolean.opBoolean","MERGE",FACE,{"derivedFrom":[makeQuery(id+"F35.boolean.opBoolean","MERGE",FACE,{"derivedFrom":[makeQuery(id+"F1.opExtrude","SWEPT_FACE",FACE,{"disambiguationData":[OSD([subQ0])]}),makeQuery(id+"F35.opExtrude","SWEPT_FACE",FACE,{"disambiguationData":[OSD([subQ0])]})]}),makeQuery(id+"F37.opExtrude","SWEPT_FACE",FACE,{"disambiguationData":[OSD([sQuery(id+"F36.wireOp",EDGE,"E69.0")])]})]});}
            extrude(context, id + "F39", {"entities" : qUnion([Q0]), "operationType" : NewBodyOperationType.ADD, "endBound" : BoundingType.UP_TO_SURFACE, "depth" : 25 * mm, "endBoundEntityFace" : qUnion([Q1]), "offsetDistance" : 25 * mm});
        }
        {
            var Q0;
            {var subQ0=sQuery(id+"F21.wireOp",EDGE,"E52.right");var subQ5=sQuery(id+"F17.wireOp",EDGE,"E37.bottom");var subQ6=makeQuery(id+"F18.opExtrude","SWEPT_FACE",FACE,{"disambiguationData":[OSD([subQ5])]});var subQ16=sQuery(id+"F21.wireOp",EDGE,"E51.right");var subQ17=makeQuery(id+"F18.boolean.opBoolean","COPY",FACE,{"derivedFrom":subQ6});var subQ18=sQuery(id+"F21.wireOp",EDGE,"E53.top");var subQ19=sQuery(id+"F21.wireOp",EDGE,"E53.right");var subQ22=sQuery(id+"F17.wireOp",EDGE,"E38.bottom");var subQ23=makeQuery(id+"F18.boolean.opBoolean","COPY",FACE,{"derivedFrom":makeQuery(id+"F18.opExtrude","SWEPT_FACE",FACE,{"disambiguationData":[OSD([subQ22])]})});var subQ24=sQuery(id+"F19.wireOp",EDGE,"E50.right");var subQ25=makeQuery(id+"F20.opExtrude","SWEPT_FACE",FACE,{"disambiguationData":[OSD([subQ24])]});var subQ26=makeQuery(id+"F20.opExtrude","CAP_EDGE",EDGE,{"disambiguationData":[OSD([subQ24])],"isStart":true});Q0=makeQuery(id+"F37.boolean.opBoolean","SPLIT",FACE,{"disambiguationData":[TD([subQ17])],"derivedFrom":makeQuery(id+"F35.boolean.opBoolean","MERGE",FACE,{"derivedFrom":[makeQuery(id+"F28.boolean.opBoolean","MERGE",FACE,{"derivedFrom":[makeQuery(id+"F23.boolean.opBoolean","MERGE",FACE,{"derivedFrom":[makeQuery(id+"F20.boolean.opBoolean","COPY",FACE,{"disambiguationData":[TD([subQ17])],"derivedFrom":subQ25}),makeQuery(id+"F20.boolean.opBoolean","COPY",FACE,{"disambiguationData":[TD([subQ23])],"derivedFrom":subQ25}),makeQuery(id+"F23.opExtrude","SWEPT_FACE",FACE,{"disambiguationData":[OSD([subQ16])]}),makeQuery(id+"F23.opExtrude","SWEPT_FACE",FACE,{"disambiguationData":[OSD([subQ0])]}),makeQuery(id+"F23.opExtrude","SWEPT_FACE",FACE,{"disambiguationData":[OSD([subQ19])]})]}),makeQuery(id+"F28.opExtrude","SWEPT_FACE",FACE,{"disambiguationData":[OSD([subQ18,subQ19])]})]}),makeQuery(id+"F35.opExtrude","SWEPT_FACE",FACE,{"disambiguationData":[OSD([subQ24]),TDD([makeQuery(id+"F20.boolean.opBoolean","COPY",EDGE,{"disambiguationData":[TD([subQ17])],"derivedFrom":subQ26})])]}),makeQuery(id+"F35.opExtrude","SWEPT_FACE",FACE,{"disambiguationData":[OSD([subQ24]),TDD([makeQuery(id+"F20.boolean.opBoolean","COPY",EDGE,{"disambiguationData":[TD([subQ23])],"derivedFrom":subQ26})])]})]})});}
            var Q1;
            {var subQ0=sQuery(id+"F21.wireOp",EDGE,"E52.right");var subQ1=sQuery(id+"F21.wireOp",EDGE,"E51.right");var subQ5=sQuery(id+"F21.wireOp",EDGE,"E53.right");var subQ6=sQuery(id+"F21.wireOp",EDGE,"E53.top");var subQ9=sQuery(id+"F17.wireOp",EDGE,"E38.bottom");var subQ10=makeQuery(id+"F18.opExtrude","SWEPT_FACE",FACE,{"disambiguationData":[OSD([subQ9])]});var subQ19=makeQuery(id+"F18.boolean.opBoolean","COPY",FACE,{"derivedFrom":subQ10});var subQ20=sQuery(id+"F19.wireOp",EDGE,"E50.right");var subQ21=makeQuery(id+"F20.opExtrude","SWEPT_FACE",FACE,{"disambiguationData":[OSD([subQ20])]});var subQ22=makeQuery(id+"F20.opExtrude","CAP_EDGE",EDGE,{"disambiguationData":[OSD([subQ20])],"isStart":true});var subQ23=sQuery(id+"F17.wireOp",EDGE,"E37.bottom");var subQ24=makeQuery(id+"F18.boolean.opBoolean","COPY",FACE,{"derivedFrom":makeQuery(id+"F18.opExtrude","SWEPT_FACE",FACE,{"disambiguationData":[OSD([subQ23])]})});Q1=makeQuery(id+"F37.boolean.opBoolean","SPLIT",FACE,{"disambiguationData":[TD([subQ19])],"derivedFrom":makeQuery(id+"F35.boolean.opBoolean","MERGE",FACE,{"derivedFrom":[makeQuery(id+"F28.boolean.opBoolean","MERGE",FACE,{"derivedFrom":[makeQuery(id+"F23.boolean.opBoolean","MERGE",FACE,{"derivedFrom":[makeQuery(id+"F20.boolean.opBoolean","COPY",FACE,{"disambiguationData":[TD([subQ24])],"derivedFrom":subQ21}),makeQuery(id+"F20.boolean.opBoolean","COPY",FACE,{"disambiguationData":[TD([subQ19])],"derivedFrom":subQ21}),makeQuery(id+"F23.opExtrude","SWEPT_FACE",FACE,{"disambiguationData":[OSD([subQ1])]}),makeQuery(id+"F23.opExtrude","SWEPT_FACE",FACE,{"disambiguationData":[OSD([subQ0])]}),makeQuery(id+"F23.opExtrude","SWEPT_FACE",FACE,{"disambiguationData":[OSD([subQ5])]})]}),makeQuery(id+"F28.opExtrude","SWEPT_FACE",FACE,{"disambiguationData":[OSD([subQ6,subQ5])]})]}),makeQuery(id+"F35.opExtrude","SWEPT_FACE",FACE,{"disambiguationData":[OSD([subQ20]),TDD([makeQuery(id+"F20.boolean.opBoolean","COPY",EDGE,{"disambiguationData":[TD([subQ24])],"derivedFrom":subQ22})])]}),makeQuery(id+"F35.opExtrude","SWEPT_FACE",FACE,{"disambiguationData":[OSD([subQ20]),TDD([makeQuery(id+"F20.boolean.opBoolean","COPY",EDGE,{"disambiguationData":[TD([subQ19])],"derivedFrom":subQ22})])]})]})});}
            var Q2;
            Q2=makeQuery(id+"F37.opExtrude","SWEPT_FACE",FACE,{"disambiguationData":[OSD([sQuery(id+"F36.wireOp",EDGE,"E74")])]});
            extrude(context, id + "F40", {"entities" : qUnion([Q0, Q1]), "operationType" : NewBodyOperationType.ADD, "endBound" : BoundingType.UP_TO_SURFACE, "depth" : 25 * mm, "endBoundEntityFace" : qUnion([Q2]), "offsetDistance" : 25 * mm});
        }
        {
            var Q0;
            {var subQ0=sQuery(id+"F17.wireOp",EDGE,"E37.top");var subQ1=sQuery(id+"F0.wireOp",EDGE,"E6.1");Q0=makeQuery(id+"F39.boolean.opBoolean","MERGE",FACE,{"derivedFrom":[makeQuery(id+"F35.opExtrude","CAP_FACE",FACE,{"disambiguationData":[OSD([sQuery(id+"F0.wireOp",EDGE,"E6.0"),subQ1,sQuery(id+"F0.wireOp",EDGE,"E6.2"),sQuery(id+"F0.wireOp",EDGE,"E6.3"),sQuery(id+"F0.wireOp",EDGE,"E6.4"),sQuery(id+"F0.wireOp",EDGE,"E6.5"),sQuery(id+"F0.wireOp",EDGE,"E6.6"),sQuery(id+"F0.wireOp",EDGE,"E6.7"),subQ0])],"isStart":false}),makeQuery(id+"F39.opExtrude","SWEPT_FACE",FACE,{"disambiguationData":[OSD([subQ1,subQ0]),TDD([makeQuery(id+"F35.opExtrude","CAP_EDGE",EDGE,{"disambiguationData":[OSD([subQ1,subQ0])],"isStart":false})])]})]});}
            var sketch = newSketch(context, id + "F41", { "sketchPlane" : qUnion([Q0])});
            skLineSegment(sketch, "E75.0", {"start": v(91.82, 52) * mm, "end": v(90.98, 52) * mm});
            skFitSpline(sketch, "E76", {"points": [v(90.98, 53.7) * mm, v(91.82, 52) * mm], "startDerivative": vector(1.82, -2.45) * mm, "endDerivative": vector(0.69, -2.65) * mm});
            skLineSegment(sketch, "E77", {"start": v(90.98, 53.7) * mm, "end": v(90.98, 52) * mm});
            skSolve(sketch);
        }
        {
            var Q0;
            Q0=makeQuery(id+"F41.imprint","IMPRINT",FACE,{"disambiguationData":[TD([[makeQuery(id+"F41.imprint","IMPRINT",EDGE,{"derivedFrom":sQuery(id+"F41.wireOp",EDGE,"E75.0")}),-1.0]])]});
            var Q1;
            {var subQ0=sQuery(id+"F17.wireOp",EDGE,"E39.right");var subQ1=sQuery(id+"F17.wireOp",EDGE,"E39.top");var subQ2=sQuery(id+"F19.wireOp",EDGE,"E49.right");var subQ3=makeQuery(id+"F20.opExtrude","CAP_FACE",FACE,{"disambiguationData":[OSD([sQuery(id+"F19.wireOp",EDGE,"E49.bottom"),sQuery(id+"F19.wireOp",EDGE,"E49.top"),sQuery(id+"F19.wireOp",EDGE,"E49.left"),subQ2])],"isStart":false});var subQ4=sQuery(id+"F17.wireOp",EDGE,"E38.bottom");var subQ5=sQuery(id+"F17.wireOp",EDGE,"E45.right");var subQ6=sQuery(id+"F17.wireOp",EDGE,"E45.left");var subQ7=sQuery(id+"F17.wireOp",EDGE,"E45.top");var subQ8=sQuery(id+"F17.wireOp",EDGE,"E45.bottom");var subQ9=makeQuery(id+"F18.opExtrude","CAP_FACE",FACE,{"disambiguationData":[OSD([subQ8,subQ7,subQ6,subQ5])],"isStart":false});var subQ10=sQuery(id+"F17.wireOp",EDGE,"E46");var subQ11=sQuery(id+"F17.wireOp",EDGE,"E41");var subQ12=makeQuery(id+"F18.opExtrude","CAP_FACE",FACE,{"disambiguationData":[OSD([subQ11,sQuery(id+"F17.wireOp",EDGE,"E42"),subQ10,sQuery(id+"F17.wireOp",EDGE,"E47")])],"isStart":false});var subQ13=sQuery(id+"F17.wireOp",EDGE,"E39.bottom");var subQ14=makeQuery(id+"F18.opExtrude","CAP_FACE",FACE,{"disambiguationData":[OSD([subQ13,subQ1,sQuery(id+"F17.wireOp",EDGE,"E39.left"),subQ0])],"isStart":false});var subQ16=sQuery(id+"F0.wireOp",EDGE,"E6.5");var subQ18=sQuery(id+"F3.wireOp",EDGE,"E12.filletArc");var subQ19=sQuery(id+"F3.wireOp",EDGE,"E9.filletArc");var subQ20=sQuery(id+"F3.wireOp",EDGE,"E8.4");var subQ21=sQuery(id+"F3.wireOp",EDGE,"E8.3");var subQ22=sQuery(id+"F3.wireOp",EDGE,"E8.2");var subQ23=sQuery(id+"F3.wireOp",EDGE,"E8.0");var subQ24=makeQuery(id+"F4.boolean.opBoolean","COPY",FACE,{"derivedFrom":makeQuery(id+"F4.opExtrude","CAP_FACE",FACE,{"disambiguationData":[OSD([subQ23,subQ22,subQ21,subQ20,subQ19,sQuery(id+"F3.wireOp",EDGE,"E10.filletArc"),sQuery(id+"F3.wireOp",EDGE,"E11"),subQ18])],"isStart":false})});var subQ25=sQuery(id+"F17.wireOp",EDGE,"E43");var subQ26=sQuery(id+"F17.wireOp",EDGE,"E37.top");var subQ27=sQuery(id+"F17.wireOp",EDGE,"E37.bottom");var subQ28=makeQuery(id+"F18.opExtrude","CAP_FACE",FACE,{"disambiguationData":[OSD([subQ27,subQ26,sQuery(id+"F17.wireOp",EDGE,"E37.left"),sQuery(id+"F17.wireOp",EDGE,"E37.right"),subQ25,sQuery(id+"F17.wireOp",EDGE,"E44")])],"isStart":false});var subQ29=sQuery(id+"F17.wireOp",EDGE,"E38.top");var subQ30=makeQuery(id+"F18.opExtrude","CAP_FACE",FACE,{"disambiguationData":[OSD([subQ4,subQ29,sQuery(id+"F17.wireOp",EDGE,"E38.left"),sQuery(id+"F17.wireOp",EDGE,"E38.right")])],"isStart":false});var subQ31=makeQuery(id+"F20.opExtrude","CAP_FACE",FACE,{"disambiguationData":[OSD([sQuery(id+"F19.wireOp",EDGE,"E50.bottom"),sQuery(id+"F19.wireOp",EDGE,"E50.top"),sQuery(id+"F19.wireOp",EDGE,"E50.left"),sQuery(id+"F19.wireOp",EDGE,"E50.right")])],"isStart":false});Q1=makeQuery(id+"F38.boolean.opBoolean","MERGE",FACE,{"derivedFrom":[makeQuery(id+"F28.boolean.opBoolean","SPLIT",FACE,{"disambiguationData":[TD([makeQuery(id+"F1.opExtrude","SWEPT_FACE",FACE,{"disambiguationData":[OSD([subQ16])]})])],"derivedFrom":makeQuery(id+"F20.boolean.opBoolean","MERGE",FACE,{"derivedFrom":[makeQuery(id+"F18.boolean.opBoolean","MERGE",FACE,{"derivedFrom":[subQ24,subQ28,subQ30,subQ14,subQ12,subQ9]}),subQ3,subQ31]})}),makeQuery(id+"F38.opExtrude","SWEPT_FACE",FACE,{"disambiguationData":[OSD([subQ0]),TDD([makeQuery(id+"F18.boolean.opBoolean","COPY",EDGE,{"derivedFrom":makeQuery(id+"F18.opExtrude","CAP_EDGE",EDGE,{"disambiguationData":[OSD([subQ0])],"isStart":false})})])]})]});}
            extrude(context, id + "F42", {"entities" : qUnion([Q0]), "operationType" : NewBodyOperationType.REMOVE, "endBound" : BoundingType.UP_TO_SURFACE, "oppositeDirection" : true, "depth" : 25 * mm, "endBoundEntityFace" : qUnion([Q1]), "offsetDistance" : 25 * mm});
        }
        {
            var Q0;
            Q0=makeQuery(id+"F35.opExtrude","CAP_FACE",FACE,{"disambiguationData":[OSD([sQuery(id+"F0.wireOp",EDGE,"E6.0"),sQuery(id+"F0.wireOp",EDGE,"E6.1"),sQuery(id+"F0.wireOp",EDGE,"E6.2"),sQuery(id+"F0.wireOp",EDGE,"E6.3"),sQuery(id+"F0.wireOp",EDGE,"E6.4"),sQuery(id+"F0.wireOp",EDGE,"E6.5"),sQuery(id+"F0.wireOp",EDGE,"E6.6"),sQuery(id+"F0.wireOp",EDGE,"E6.7"),sQuery(id+"F17.wireOp",EDGE,"E45.right"),sQuery(id+"F32.wireOp",EDGE,"E64.bottom"),sQuery(id+"F32.wireOp",EDGE,"E64.top"),sQuery(id+"F32.wireOp",EDGE,"E64.left"),sQuery(id+"F32.wireOp",EDGE,"E64.right")])],"isStart":false});
            var sketch = newSketch(context, id + "F43", { "sketchPlane" : qUnion([Q0])});
            skPoint(sketch, "E78", {"position": v(91.82, 0.15) * mm});
            skFitSpline(sketch, "E79", {"points": [v(87.99, -1.87) * mm, v(91.82, 0.15) * mm], "startDerivative": vector(5.93, 1.3) * mm, "endDerivative": vector(0.54, 1.6) * mm});
            skLineSegment(sketch, "E80", {"start": v(91.82, 0.15) * mm, "end": v(90.74, 0.15) * mm});
            skLineSegment(sketch, "E81", {"start": v(90.74, 0.15) * mm, "end": v(87.99, -1.87) * mm});
            skSolve(sketch);
        }
        {
            var Q0;
            Q0=makeQuery(id+"F43.imprint","IMPRINT",FACE,{"disambiguationData":[TD([[makeQuery(id+"F43.imprint","IMPRINT",EDGE,{"derivedFrom":sQuery(id+"F43.wireOp",EDGE,"E79")}),1.0]])]});
            var Q1;
            {var subQ0=sQuery(id+"F19.wireOp",EDGE,"E50.right");var subQ1=sQuery(id+"F19.wireOp",EDGE,"E50.left");var subQ2=sQuery(id+"F19.wireOp",EDGE,"E50.top");var subQ3=sQuery(id+"F19.wireOp",EDGE,"E50.bottom");var subQ4=sQuery(id+"F19.wireOp",EDGE,"E49.right");var subQ5=sQuery(id+"F19.wireOp",EDGE,"E49.left");var subQ6=sQuery(id+"F19.wireOp",EDGE,"E49.top");var subQ7=sQuery(id+"F19.wireOp",EDGE,"E49.bottom");var subQ8=sQuery(id+"F17.wireOp",EDGE,"E47");var subQ9=sQuery(id+"F17.wireOp",EDGE,"E46");var subQ10=sQuery(id+"F17.wireOp",EDGE,"E45.right");var subQ11=sQuery(id+"F17.wireOp",EDGE,"E45.left");var subQ12=sQuery(id+"F17.wireOp",EDGE,"E45.top");var subQ13=sQuery(id+"F17.wireOp",EDGE,"E45.bottom");var subQ14=sQuery(id+"F17.wireOp",EDGE,"E44");var subQ15=sQuery(id+"F17.wireOp",EDGE,"E43");var subQ16=sQuery(id+"F17.wireOp",EDGE,"E42");var subQ17=sQuery(id+"F17.wireOp",EDGE,"E41");var subQ18=sQuery(id+"F17.wireOp",EDGE,"E39.right");var subQ19=sQuery(id+"F17.wireOp",EDGE,"E39.left");var subQ20=sQuery(id+"F17.wireOp",EDGE,"E39.top");var subQ21=sQuery(id+"F17.wireOp",EDGE,"E39.bottom");var subQ22=sQuery(id+"F17.wireOp",EDGE,"E38.right");var subQ23=sQuery(id+"F17.wireOp",EDGE,"E38.left");var subQ24=sQuery(id+"F17.wireOp",EDGE,"E38.top");var subQ25=sQuery(id+"F17.wireOp",EDGE,"E38.bottom");var subQ26=sQuery(id+"F17.wireOp",EDGE,"E37.right");var subQ27=sQuery(id+"F17.wireOp",EDGE,"E37.left");var subQ28=sQuery(id+"F17.wireOp",EDGE,"E37.top");var subQ29=sQuery(id+"F17.wireOp",EDGE,"E37.bottom");var subQ30=sQuery(id+"F3.wireOp",EDGE,"E12.filletArc");var subQ31=sQuery(id+"F3.wireOp",EDGE,"E11");var subQ32=sQuery(id+"F3.wireOp",EDGE,"E10.filletArc");var subQ33=sQuery(id+"F3.wireOp",EDGE,"E9.filletArc");var subQ34=sQuery(id+"F3.wireOp",EDGE,"E8.4");var subQ35=sQuery(id+"F3.wireOp",EDGE,"E8.3");var subQ36=sQuery(id+"F3.wireOp",EDGE,"E8.2");var subQ37=sQuery(id+"F3.wireOp",EDGE,"E8.0");var subQ38=makeQuery(id+"F20.opExtrude","CAP_FACE",FACE,{"disambiguationData":[OSD([subQ7,subQ6,subQ5,subQ4])],"isStart":false});var subQ39=makeQuery(id+"F18.opExtrude","CAP_FACE",FACE,{"disambiguationData":[OSD([subQ13,subQ12,subQ11,subQ10])],"isStart":false});var subQ40=makeQuery(id+"F18.opExtrude","CAP_FACE",FACE,{"disambiguationData":[OSD([subQ17,subQ16,subQ9,subQ8])],"isStart":false});var subQ41=makeQuery(id+"F18.opExtrude","CAP_FACE",FACE,{"disambiguationData":[OSD([subQ21,subQ20,subQ19,subQ18])],"isStart":false});var subQ43=sQuery(id+"F0.wireOp",EDGE,"E6.5");var subQ45=makeQuery(id+"F4.boolean.opBoolean","COPY",FACE,{"derivedFrom":makeQuery(id+"F4.opExtrude","CAP_FACE",FACE,{"disambiguationData":[OSD([subQ37,subQ36,subQ35,subQ34,subQ33,subQ32,subQ31,subQ30])],"isStart":false})});var subQ46=makeQuery(id+"F18.opExtrude","CAP_FACE",FACE,{"disambiguationData":[OSD([subQ29,subQ28,subQ27,subQ26,subQ15,subQ14])],"isStart":false});var subQ47=makeQuery(id+"F18.opExtrude","CAP_FACE",FACE,{"disambiguationData":[OSD([subQ25,subQ24,subQ23,subQ22])],"isStart":false});var subQ48=makeQuery(id+"F20.opExtrude","CAP_FACE",FACE,{"disambiguationData":[OSD([subQ3,subQ2,subQ1,subQ0])],"isStart":false});Q1=makeQuery(id+"F42.boolean.opBoolean","MERGE",FACE,{"derivedFrom":[makeQuery(id+"F38.boolean.opBoolean","MERGE",FACE,{"derivedFrom":[makeQuery(id+"F28.boolean.opBoolean","SPLIT",FACE,{"disambiguationData":[TD([makeQuery(id+"F1.opExtrude","SWEPT_FACE",FACE,{"disambiguationData":[OSD([subQ43])]})])],"derivedFrom":makeQuery(id+"F20.boolean.opBoolean","MERGE",FACE,{"derivedFrom":[makeQuery(id+"F18.boolean.opBoolean","MERGE",FACE,{"derivedFrom":[subQ45,subQ46,subQ47,subQ41,subQ40,subQ39]}),subQ38,subQ48]})}),makeQuery(id+"F38.opExtrude","SWEPT_FACE",FACE,{"disambiguationData":[OSD([subQ18]),TDD([makeQuery(id+"F18.boolean.opBoolean","COPY",EDGE,{"derivedFrom":makeQuery(id+"F18.opExtrude","CAP_EDGE",EDGE,{"disambiguationData":[OSD([subQ18])],"isStart":false})})])]})]}),makeQuery(id+"F42.opExtrude","CAP_FACE",FACE,{"disambiguationData":[OSD([subQ37,subQ36,subQ35,subQ34,subQ33,subQ32,subQ31,subQ30,subQ29,subQ28,subQ27,subQ26,subQ25,subQ24,subQ23,subQ22,subQ21,subQ20,subQ19,subQ18,subQ17,subQ16,subQ15,subQ14,subQ13,subQ12,subQ11,subQ10,subQ9,subQ8,subQ7,subQ6,subQ5,subQ4,subQ3,subQ2,subQ1,subQ0])],"isStart":false})]});}
            extrude(context, id + "F44", {"entities" : qUnion([Q0]), "operationType" : NewBodyOperationType.REMOVE, "endBound" : BoundingType.UP_TO_SURFACE, "oppositeDirection" : true, "depth" : 25 * mm, "endBoundEntityFace" : qUnion([Q1]), "offsetDistance" : 25 * mm});
        }
    });
